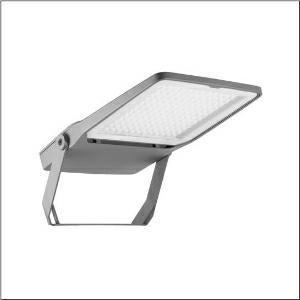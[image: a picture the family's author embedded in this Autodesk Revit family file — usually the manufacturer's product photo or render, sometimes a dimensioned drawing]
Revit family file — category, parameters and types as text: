
# Revit family: floodlight_fl_20_midi___pl43_5xa7682e1a1ac_2750
name_source: partatom
category: Lighting Fixtures
units: mm (PartAtom-declared; Revit-internal decimal feet)

## family parameters
Cut with Voids When Loaded = No
Host = Face
Light Source = No
Part Type = Normal
Room Calculation Point = No
Round Connector Dimension = Use Diameter
Shared = No

## types (1)
- --- (1 x LED 3000K / CRI = 80 (unbekannt), 22300 lm, 3000K)
    Apparent Load = 208 VA
    CIE Flux Codes = 32 74 99 100 100
    Color Rendering = 80
    Color Temperature = 3000K
    Default Elevation = 1800 mm
    Description = Floodlight FL 20 midi, floodlight, primary light control with lens, of plastic, primary optical cover: protective disc, of toughened safety glass, transparent, light distribution: PL43, light emission: direct distribution, primary light characteristic: asymmetric, installation type: surface-mounted, LED High Power LED, rated luminous flux: 22.300 lm, light colour: 830, colour temperature: 3000K, control gear: ECG Plus, control: flexible luminous flux parameterisation, time-dependent luminous flux control, digital communication interface, power reduction, overheat protection, electronic power reduction, with terminal, 5-pole, max. 2.5mm², mains connection: 220..240V, AC, 50/60Hz, rated input power: 208W, LED unit, of diecast aluminium, powder-coated, Siteco® metallic grey (DB 702S), length: 654 mm, width: 450 mm, height: 76mm, housing frame, of diecast aluminium, powder-coated, Siteco® metallic grey (DB 702S), mounting bracket, of steel, powder-coated, Siteco® metallic grey (DB 702S), DALIprotection rating (complete): IP66, insulation class (complete): insulation class II (safety insulation), certification: CE, ENEC, VDE, protection symbol: D, permissible ambient temperature for indoor applications: -40..+40°C, permissible ambient temperature for outdoor applications: -40..+50°C, standard: DIN EN 12944, packaging unit: 1 piece

Light Distribution: PL43
    Height = 76 mm
    Lamp = 1 x LED 3000K / CRI >= 80 (unbekannt)
    Lamp Light Flux = 22300 lm
    Lamp count = 1
    Length = 672 mm
    Luminous efficacy = 107 lm/W
    Manufacturer = Siteco
    ModVariant = No
    Model = 5XA7682E1A1AC
    Number of Poles = 1
    OnlyDefault = Yes
    Power Factor = 1
    Product Name = Floodlight FL 20 midi | PL43
    Product group = floodlight | pylon top
    ProductGroupID = 6101
    Protection Class = Protection class II
    Protection Degree = IP 66
    RLX_Detail_Level = 1
    RlxData = <blob elided: 97297 chars, md5=af1dbe7f>
    Socket = socket
    Standby Power = 0 W
    System Light Flux = 22300 lm
    System Power = 208 W
    Type Comments = factory setting: luminous flux: 100 % | dim-lin: 254 | 484 mA
    Type Image = l_1005943.jpg
    URL = http://relux.com
    VarID = @adj_143803
    Voltage = 0 V
    Weight = 0.00 kg
    Width = 450 mm

## geometry (parser evidence)
native form markers: Blend x4, Sweep x12
no freeform markers — native parametric forms only
